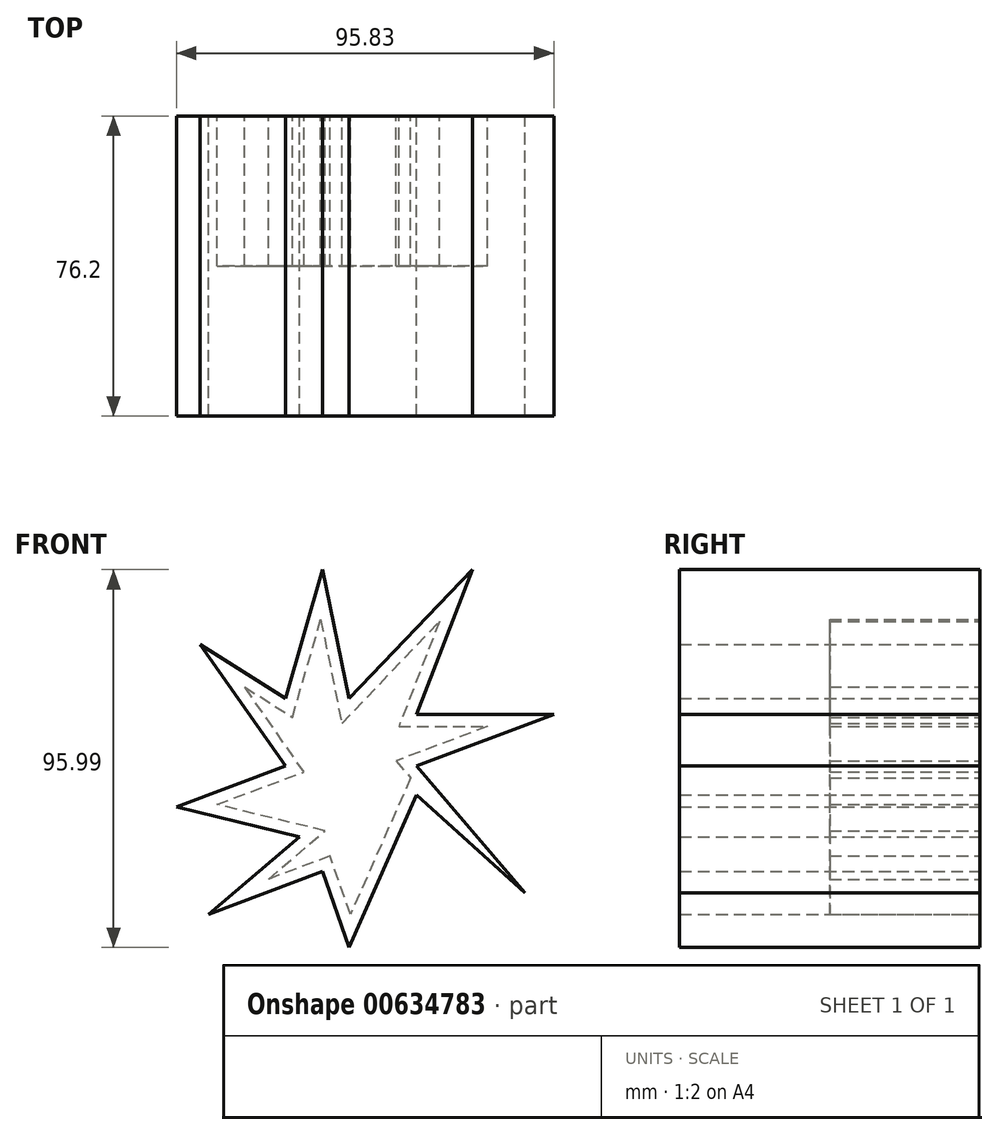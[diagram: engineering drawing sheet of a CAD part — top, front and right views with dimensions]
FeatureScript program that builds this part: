
annotation { "Feature Type Name" : "Feature", "Feature Type Description" : "" }
export const myFeature = defineFeature(function(context is Context, id is Id, definition is map)
    precondition{}
    {
        {
            var Q0;
            Q0=qCreatedBy(makeId("Front.planeOp"),FACE);
            var sketch = newSketch(context, id + "F0", { "sketchPlane" : qUnion([Q0])});
            skLineSegment(sketch, "E0", {"start": v(0, -42.02) * mm, "end": v(0, -46.06) * mm});
            skLineSegment(sketch, "E1", {"start": v(0, -46.06) * mm, "end": v(17.08, -7.33) * mm});
            skLineSegment(sketch, "E2", {"start": v(17.08, -7.33) * mm, "end": v(44.64, -32.28) * mm});
            skLineSegment(sketch, "E3", {"start": v(44.64, -32.28) * mm, "end": v(17.08, 0) * mm});
            skLineSegment(sketch, "E4", {"start": v(17.08, 0) * mm, "end": v(52, 13.1) * mm});
            skLineSegment(sketch, "E5", {"start": v(52, 13.1) * mm, "end": v(17.08, 13.1) * mm});
            skLineSegment(sketch, "E6", {"start": v(17.08, 13.1) * mm, "end": v(31.34, 49.93) * mm});
            skLineSegment(sketch, "E7", {"start": v(31.34, 49.93) * mm, "end": v(0, 17.14) * mm});
            skLineSegment(sketch, "E8", {"start": v(0, 17.14) * mm, "end": v(-6.68, 49.93) * mm});
            skLineSegment(sketch, "E9", {"start": v(-6.68, 49.93) * mm, "end": v(-16.18, 17.14) * mm});
            skLineSegment(sketch, "E10", {"start": v(-16.18, 17.14) * mm, "end": v(-37.8, 30.92) * mm});
            skLineSegment(sketch, "E11", {"start": v(-37.8, 30.92) * mm, "end": v(-16.18, 0) * mm});
            skLineSegment(sketch, "E12", {"start": v(-16.18, 0) * mm, "end": v(-43.82, -10.37) * mm});
            skLineSegment(sketch, "E13", {"start": v(-43.82, -10.37) * mm, "end": v(-12.62, -18.02) * mm});
            skLineSegment(sketch, "E14", {"start": v(-12.62, -18.02) * mm, "end": v(-35.65, -37.69) * mm});
            skLineSegment(sketch, "E15", {"start": v(-35.65, -37.69) * mm, "end": v(-6.68, -26.82) * mm});
            skLineSegment(sketch, "E16", {"start": v(-6.68, -26.82) * mm, "end": v(0, -46.06) * mm});
            skSolve(sketch);
        }
        {
            var Q0;
            Q0=makeQuery(id+"F0.imprint","IMPRINT",FACE,{"disambiguationData":[TD([[makeQuery(id+"F0.imprint","IMPRINT",EDGE,{"derivedFrom":sQuery(id+"F0.wireOp",EDGE,"E1")}),1.0]])]});
            extrude(context, id + "F1", {"entities" : qUnion([Q0]), "depth" : 76.2 * mm, "offsetDistance" : 25.4 * mm});
        }
        {
            var Q0;
            Q0=makeQuery(id+"F1.opExtrude","CAP_FACE",FACE,{"disambiguationData":[OSD([sQuery(id+"F0.wireOp",EDGE,"E1"),sQuery(id+"F0.wireOp",EDGE,"E2"),sQuery(id+"F0.wireOp",EDGE,"E3"),sQuery(id+"F0.wireOp",EDGE,"E4"),sQuery(id+"F0.wireOp",EDGE,"E5"),sQuery(id+"F0.wireOp",EDGE,"E6"),sQuery(id+"F0.wireOp",EDGE,"E7"),sQuery(id+"F0.wireOp",EDGE,"E8"),sQuery(id+"F0.wireOp",EDGE,"E9"),sQuery(id+"F0.wireOp",EDGE,"E10"),sQuery(id+"F0.wireOp",EDGE,"E11"),sQuery(id+"F0.wireOp",EDGE,"E12"),sQuery(id+"F0.wireOp",EDGE,"E13"),sQuery(id+"F0.wireOp",EDGE,"E14"),sQuery(id+"F0.wireOp",EDGE,"E15"),sQuery(id+"F0.wireOp",EDGE,"E16")])],"isStart":true});
            var sketch = newSketch(context, id + "F2", { "sketchPlane" : qUnion([Q0])});
            skLineSegment(sketch, "E17.0", {"start": v(-15.65, -3.02) * mm, "end": v(-0.34, -37.74) * mm});
            skLineSegment(sketch, "E17.1", {"start": v(-11.94, 1.33) * mm, "end": v(-15.65, -3.02) * mm});
            skLineSegment(sketch, "E17.2", {"start": v(-35.2, 10.05) * mm, "end": v(-11.94, 1.33) * mm});
            skLineSegment(sketch, "E17.3", {"start": v(-12.63, 10.05) * mm, "end": v(-35.2, 10.05) * mm});
            skLineSegment(sketch, "E17.4", {"start": v(33.52, -9.76) * mm, "end": v(11.43, -1.47) * mm});
            skLineSegment(sketch, "E17.5", {"start": v(6.12, -16.48) * mm, "end": v(33.52, -9.76) * mm});
            skLineSegment(sketch, "E17.6", {"start": v(20.47, -28.74) * mm, "end": v(6.12, -16.48) * mm});
            skLineSegment(sketch, "E17.7", {"start": v(4.82, -22.87) * mm, "end": v(20.47, -28.74) * mm});
            skLineSegment(sketch, "E17.8", {"start": v(11.43, -1.47) * mm, "end": v(26.53, 20.12) * mm});
            skLineSegment(sketch, "E17.9", {"start": v(26.53, 20.12) * mm, "end": v(14.39, 12.38) * mm});
            skLineSegment(sketch, "E17.10", {"start": v(14.39, 12.38) * mm, "end": v(7.2, 37.2) * mm});
            skLineSegment(sketch, "E17.11", {"start": v(7.2, 37.2) * mm, "end": v(1.82, 10.82) * mm});
            skLineSegment(sketch, "E17.12", {"start": v(-0.34, -37.74) * mm, "end": v(4.82, -22.87) * mm});
            skLineSegment(sketch, "E17.13", {"start": v(1.82, 10.82) * mm, "end": v(-22.97, 36.77) * mm});
            skLineSegment(sketch, "E17.14", {"start": v(-22.97, 36.77) * mm, "end": v(-12.63, 10.05) * mm});
            skSolve(sketch);
        }
        {
            var Q0;
            Q0=makeQuery(id+"F2.imprint","IMPRINT",FACE,{"disambiguationData":[TD([[makeQuery(id+"F2.imprint","IMPRINT",EDGE,{"derivedFrom":sQuery(id+"F2.wireOp",EDGE,"E17.0")}),1.0]])]});
            extrude(context, id + "F3", {"entities" : qUnion([Q0]), "operationType" : NewBodyOperationType.REMOVE, "oppositeDirection" : true, "depth" : 38.1 * mm, "offsetDistance" : 25.4 * mm});
        }
    });
